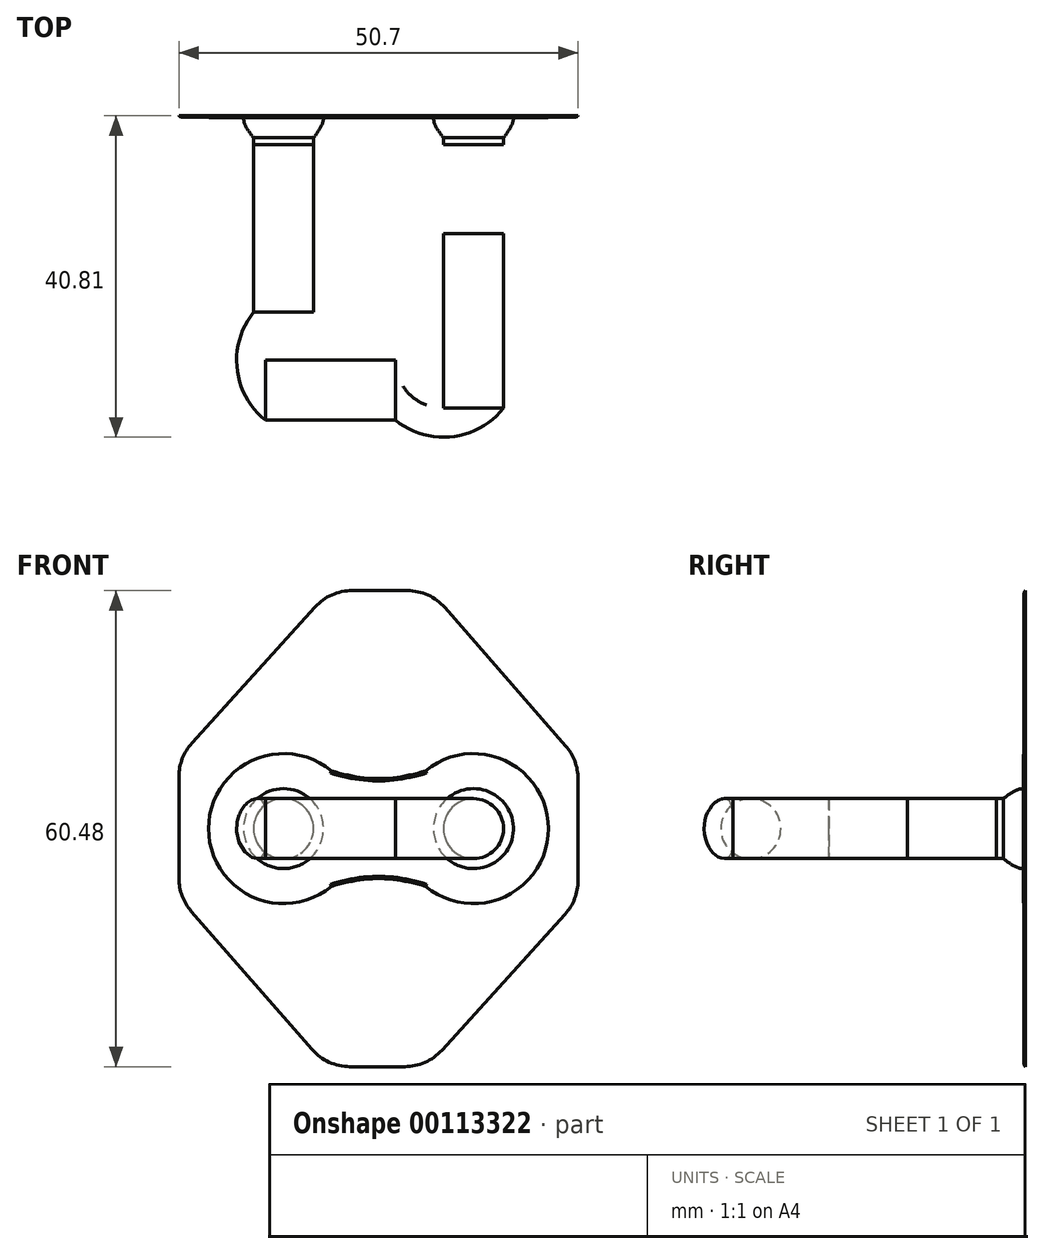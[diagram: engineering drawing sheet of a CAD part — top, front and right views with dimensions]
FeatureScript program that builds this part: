
annotation { "Feature Type Name" : "Feature", "Feature Type Description" : "" }
export const myFeature = defineFeature(function(context is Context, id is Id, definition is map)
    precondition{}
    {
        {
            var Q0;
            Q0=qCreatedBy(makeId("Front.planeOp"),FACE);
            var sketch = newSketch(context, id + "F0", { "sketchPlane" : qUnion([Q0])});
            skLineSegment(sketch, "E0.bottom", {"start": v(-25.35, 30.24) * mm, "end": v(-6.16, 30.24) * mm, "construction": true});
            skLineSegment(sketch, "E0.top", {"start": v(-25.35, -30.24) * mm, "end": v(-6.54, -30.24) * mm, "construction": true});
            skLineSegment(sketch, "E0.left", {"start": v(-25.35, 30.24) * mm, "end": v(-25.35, 9.06) * mm, "construction": true});
            skLineSegment(sketch, "E0.right", {"start": v(25.35, 30.24) * mm, "end": v(25.35, 8.72) * mm, "construction": true});
            skLineSegment(sketch, "E1", {"start": v(-25.35, 30.24) * mm, "end": v(-16.12, 19.24) * mm, "construction": true});
            skLineSegment(sketch, "E2", {"start": v(25.35, 30.24) * mm, "end": v(16.14, 19.25) * mm, "construction": true});
            skLineSegment(sketch, "E3", {"start": v(0, 0) * mm, "end": v(16.12, -19.24) * mm});
            skLineSegment(sketch, "E4", {"start": v(6.54, 30.24) * mm, "end": v(25.35, 30.24) * mm, "construction": true});
            skLineSegment(sketch, "E5", {"start": v(25.35, 6.34) * mm, "end": v(25.35, -6.61) * mm});
            skLineSegment(sketch, "E6", {"start": v(8.44, 28.06) * mm, "end": v(16.14, 19.25) * mm});
            skLineSegment(sketch, "E7", {"start": v(-3.34, 30.24) * mm, "end": v(3.66, 30.24) * mm});
            skLineSegment(sketch, "E8", {"start": v(-25.35, 6.61) * mm, "end": v(-25.35, -6.34) * mm});
            skLineSegment(sketch, "E9", {"start": v(-25.35, -8.72) * mm, "end": v(-25.35, -30.24) * mm, "construction": true});
            skLineSegment(sketch, "E10", {"start": v(-3.66, -30.24) * mm, "end": v(3.34, -30.24) * mm});
            skLineSegment(sketch, "E11", {"start": v(6.16, -30.24) * mm, "end": v(25.35, -30.24) * mm, "construction": true});
            skLineSegment(sketch, "E12", {"start": v(25.35, -9.06) * mm, "end": v(25.35, -30.24) * mm, "construction": true});
            skLineSegment(sketch, "E13", {"start": v(-8.05, 28.15) * mm, "end": v(-16.12, 19.24) * mm});
            skLineSegment(sketch, "E14", {"start": v(-23.78, -10.51) * mm, "end": v(-8.44, -28.06) * mm});
            skLineSegment(sketch, "E15", {"start": v(8.05, -28.15) * mm, "end": v(23.7, -10.88) * mm});
            skLineSegment(sketch, "E16", {"start": v(16.12, -19.24) * mm, "end": v(25.35, -30.24) * mm, "construction": true});
            skLineSegment(sketch, "E17", {"start": v(16.14, 19.25) * mm, "end": v(23.78, 10.51) * mm});
            skLineSegment(sketch, "E18", {"start": v(-16.12, 19.24) * mm, "end": v(-23.7, 10.88) * mm});
            skLineSegment(sketch, "E19", {"start": v(-16.14, -19.25) * mm, "end": v(-25.35, -30.24) * mm, "construction": true});
            skLineSegment(sketch, "E20", {"start": v(-16.12, 19.24) * mm, "end": v(0, 0) * mm});
            skLineSegment(sketch, "E21", {"start": v(16.14, 19.25) * mm, "end": v(-16.14, -19.25) * mm});
            skPoint(sketch, "E22.visualSharp", {"position": v(-6.16, 30.24) * mm});
            skArc(sketch, "E22.filletArc", {"start": v(-3.34, 30.24) * mm, "mid": v(-5.92, 29.7) * mm, "end": v(-8.05, 28.15) * mm});
            skPoint(sketch, "E23.visualSharp", {"position": v(6.54, 30.24) * mm});
            skArc(sketch, "E23.filletArc", {"start": v(8.44, 28.06) * mm, "mid": v(6.28, 29.67) * mm, "end": v(3.66, 30.24) * mm});
            skPoint(sketch, "E24.visualSharp", {"position": v(25.35, 8.72) * mm});
            skArc(sketch, "E24.filletArc", {"start": v(25.35, 6.34) * mm, "mid": v(24.94, 8.57) * mm, "end": v(23.78, 10.51) * mm});
            skPoint(sketch, "E25.visualSharp", {"position": v(25.35, -9.06) * mm});
            skArc(sketch, "E25.filletArc", {"start": v(23.7, -10.88) * mm, "mid": v(24.92, -8.9) * mm, "end": v(25.35, -6.61) * mm});
            skPoint(sketch, "E26.visualSharp", {"position": v(6.16, -30.24) * mm});
            skArc(sketch, "E26.filletArc", {"start": v(3.34, -30.24) * mm, "mid": v(5.92, -29.7) * mm, "end": v(8.05, -28.15) * mm});
            skPoint(sketch, "E27.visualSharp", {"position": v(-6.54, -30.24) * mm});
            skArc(sketch, "E27.filletArc", {"start": v(-8.44, -28.06) * mm, "mid": v(-6.28, -29.67) * mm, "end": v(-3.66, -30.24) * mm});
            skPoint(sketch, "E28.visualSharp", {"position": v(-25.35, -8.72) * mm});
            skArc(sketch, "E28.filletArc", {"start": v(-25.35, -6.34) * mm, "mid": v(-24.94, -8.57) * mm, "end": v(-23.78, -10.51) * mm});
            skPoint(sketch, "E29.visualSharp", {"position": v(-25.35, 9.06) * mm});
            skArc(sketch, "E29.filletArc", {"start": v(-23.7, 10.88) * mm, "mid": v(-24.92, 8.9) * mm, "end": v(-25.35, 6.61) * mm});
            skSolve(sketch);
        }
        {
            assignVariable(context, id + "F1", {"name" : "RealDistance", "anyValue" : .15});
        }
        {
            var Q0;
            Q0=qSketchRegion(id+"F0",true);
            extrude(context, id + "F2", {"entities" : qUnion([Q0]), "depth" : (getVariable(context, 'RealDistance')) * mm});
        }
        {
            assignVariable(context, id + "F3", {"name" : "FilletBase", "anyValue" : .5});
        }
        {
            var Q0;
            Q0=makeQuery(id+"F2.opExtrude","CAP_EDGE",EDGE,{"disambiguationData":[OSD([sQuery(id+"F0.wireOp",EDGE,"E5")])],"isStart":false});
            fillet(context, id + "F4", {"entities" : qUnion([Q0]), "radius" : (getVariable(context, 'FilletBase')) * mm, "tangentPropagation" : true, "allowEdgeOverflow" : false});
        }
        {
            var Q0;
            Q0=makeQuery(id+"F2.opExtrude","CAP_FACE",FACE,{"disambiguationData":[OSD([sQuery(id+"F0.wireOp",EDGE,"E5"),sQuery(id+"F0.wireOp",EDGE,"E6"),sQuery(id+"F0.wireOp",EDGE,"E7"),sQuery(id+"F0.wireOp",EDGE,"E8"),sQuery(id+"F0.wireOp",EDGE,"E10"),sQuery(id+"F0.wireOp",EDGE,"E13"),sQuery(id+"F0.wireOp",EDGE,"E14"),sQuery(id+"F0.wireOp",EDGE,"E15"),sQuery(id+"F0.wireOp",EDGE,"E17"),sQuery(id+"F0.wireOp",EDGE,"E18"),sQuery(id+"F0.wireOp",EDGE,"E22.filletArc"),sQuery(id+"F0.wireOp",EDGE,"E23.filletArc"),sQuery(id+"F0.wireOp",EDGE,"E24.filletArc"),sQuery(id+"F0.wireOp",EDGE,"E25.filletArc"),sQuery(id+"F0.wireOp",EDGE,"E26.filletArc"),sQuery(id+"F0.wireOp",EDGE,"E27.filletArc"),sQuery(id+"F0.wireOp",EDGE,"E28.filletArc"),sQuery(id+"F0.wireOp",EDGE,"E29.filletArc")])],"isStart":false});
            var sketch = newSketch(context, id + "F5", { "sketchPlane" : qUnion([Q0])});
            skCircle(sketch, "E30", {"center": v(-12.06, 0) * mm, "radius": 9.53 * mm});
            skCircle(sketch, "E31", {"center": v(12.07, 0) * mm, "radius": 9.53 * mm});
            skLineSegment(sketch, "E32", {"start": v(0, 6.35) * mm, "end": v(0, -6.35) * mm, "construction": true});
            skLineSegment(sketch, "E33", {"start": v(-12.06, 9.53) * mm, "end": v(0, 9.53) * mm, "construction": true});
            skLineSegment(sketch, "E34", {"start": v(-12.07, -9.53) * mm, "end": v(0, -9.53) * mm, "construction": true});
            skLineSegment(sketch, "E35", {"start": v(-12.06, 9.53) * mm, "end": v(-12.06, 0) * mm, "construction": true});
            skLineSegment(sketch, "E36", {"start": v(-12.07, 0) * mm, "end": v(-12.07, -9.53) * mm, "construction": true});
            skLineSegment(sketch, "E37", {"start": v(12.07, -9.53) * mm, "end": v(12.07, 0) * mm, "construction": true});
            skLineSegment(sketch, "E38", {"start": v(12.07, 9.53) * mm, "end": v(12.07, 0) * mm, "construction": true});
            skLineSegment(sketch, "E39", {"start": v(0, 9.53) * mm, "end": v(12.07, 9.53) * mm, "construction": true});
            skLineSegment(sketch, "E40", {"start": v(0, -9.53) * mm, "end": v(12.07, -9.53) * mm, "construction": true});
            skFitSpline(sketch, "E41", {"points": [v(-12.06, 9.53) * mm, v(0, 6.35) * mm, v(12.07, 9.53) * mm], "startDerivative": vector(24.13, -9.53) * mm, "endDerivative": vector(24.13, 9.52) * mm});
            skFitSpline(sketch, "E42", {"points": [v(-12.07, -9.53) * mm, v(0, -6.35) * mm, v(12.07, -9.53) * mm], "startDerivative": vector(24.13, 9.52) * mm, "endDerivative": vector(24.13, -9.52) * mm});
            skSolve(sketch);
        }
        {
            assignVariable(context, id + "F6", {"name" : "RealDistancePlatform", "anyValue" : .1});
        }
        {
            var Q0;
            Q0=qSketchRegion(id+"F5",true);
            extrude(context, id + "F7", {"entities" : qUnion([Q0]), "operationType" : NewBodyOperationType.ADD, "depth" : (getVariable(context, 'RealDistancePlatform')) * mm});
        }
        {
            var Q0;
            Q0=makeQuery(id+"F7.opExtrude","CAP_EDGE",EDGE,{"disambiguationData":[OSD([sQuery(id+"F5.wireOp",EDGE,"E31")])],"isStart":false});
            var Q1;
            Q1=makeQuery(id+"F7.opExtrude","CAP_EDGE",EDGE,{"disambiguationData":[OSD([sQuery(id+"F5.wireOp",EDGE,"E42")])],"isStart":false});
            var Q2;
            Q2=makeQuery(id+"F7.opExtrude","CAP_EDGE",EDGE,{"disambiguationData":[OSD([sQuery(id+"F5.wireOp",EDGE,"E30")])],"isStart":false});
            var Q3;
            Q3=makeQuery(id+"F7.opExtrude","CAP_EDGE",EDGE,{"disambiguationData":[OSD([sQuery(id+"F5.wireOp",EDGE,"E41")])],"isStart":false});
            fillet(context, id + "F8", {"entities" : qUnion([Q0, Q1, Q2, Q3]), "radius" : (getVariable(context, 'FilletBase')) * mm, "tangentPropagation" : true, "allowEdgeOverflow" : false});
        }
        {
            var Q0;
            Q0=makeQuery(id+"F7.opExtrude","CAP_FACE",FACE,{"disambiguationData":[OSD([sQuery(id+"F5.wireOp",EDGE,"E30"),sQuery(id+"F5.wireOp",EDGE,"E31"),sQuery(id+"F5.wireOp",EDGE,"E41"),sQuery(id+"F5.wireOp",EDGE,"E42")])],"isStart":false});
            var sketch = newSketch(context, id + "F9", { "sketchPlane" : qUnion([Q0])});
            skCircle(sketch, "E43", {"center": v(-12.06, 0) * mm, "radius": 5.08 * mm});
            skCircle(sketch, "E44", {"center": v(12.07, 0) * mm, "radius": 5.08 * mm});
            skSolve(sketch);
        }
        {
            var Q0;
            Q0=makeQuery(id+"F9.imprint","IMPRINT",FACE,{"disambiguationData":[TD([[makeQuery(id+"F9.imprint","IMPRINT",EDGE,{"derivedFrom":sQuery(id+"F9.wireOp",EDGE,"E43")}),-1.0]])]});
            cPlane(context, id + "F10", {"entities" : qUnion([Q0]), "cplaneType" : CPlaneType.OFFSET, "offset" : 2.54 * mm, "width" : 152.4 * mm, "height" : 152.4 * mm});
        }
        {
            var Q0;
            Q0=qCreatedBy(id+"F10.planeOp",FACE);
            var sketch = newSketch(context, id + "F11", { "sketchPlane" : qUnion([Q0])});
            skCircle(sketch, "E45", {"center": v(-12.06, 0) * mm, "radius": 3.81 * mm});
            skCircle(sketch, "E46", {"center": v(12.07, 0) * mm, "radius": 3.81 * mm});
            skSolve(sketch);
        }
        {
            var Q0;
            Q0=makeQuery(id+"F9.imprint","IMPRINT",FACE,{"disambiguationData":[TD([[makeQuery(id+"F9.imprint","IMPRINT",EDGE,{"derivedFrom":sQuery(id+"F9.wireOp",EDGE,"E43")}),1.0]])]});
            var Q1;
            Q1=makeQuery(id+"F11.imprint","IMPRINT",FACE,{"disambiguationData":[TD([[makeQuery(id+"F11.imprint","IMPRINT",EDGE,{"derivedFrom":sQuery(id+"F11.wireOp",EDGE,"E45")}),1.0]])]});
            loft(context, id + "F12", {"startCondition" : LoftEndDerivativeType.NORMAL_TO_PROFILE, "startMagnitude" : 1, "sheetProfilesArray" : [{ "sheetProfileEntities" : qUnion([Q0]) }, { "sheetProfileEntities" : qUnion([Q1]) }]});
        }
        {
            var Q1;
            Q1=makeQuery(id+"F9.imprint","IMPRINT",FACE,{"disambiguationData":[TD([[makeQuery(id+"F9.imprint","IMPRINT",EDGE,{"derivedFrom":sQuery(id+"F9.wireOp",EDGE,"E44")}),1.0]])]});
            var Q2;
            Q2=makeQuery(id+"F11.imprint","IMPRINT",FACE,{"disambiguationData":[TD([[makeQuery(id+"F11.imprint","IMPRINT",EDGE,{"derivedFrom":sQuery(id+"F11.wireOp",EDGE,"E46")}),1.0]])]});
            loft(context, id + "F13", {"operationType" : NewBodyOperationType.ADD, "startCondition" : LoftEndDerivativeType.NORMAL_TO_PROFILE, "startMagnitude" : 1, "sheetProfilesArray" : [{ "sheetProfileEntities" : qUnion([Q1]) }, { "sheetProfileEntities" : qUnion([Q2]) }]});
        }
        {
            assignVariable(context, id + "F14", {"name" : "ExLockBar", "anyValue" : .8725});
        }
        {
            var Q0;
            Q0=makeQuery(id+"F13.opLoft","CAP_FACE",FACE,{"disambiguationData":[OSD([makeQuery(id+"F11.imprint","IMPRINT",FACE,{"disambiguationData":[TD([[makeQuery(id+"F11.imprint","IMPRINT",EDGE,{"derivedFrom":sQuery(id+"F11.wireOp",EDGE,"E46")}),1.0]])]})])],"isStart":true});
            var Q1;
            Q1=makeQuery(id+"F12.opLoft","CAP_FACE",FACE,{"disambiguationData":[OSD([makeQuery(id+"F11.imprint","IMPRINT",FACE,{"disambiguationData":[TD([[makeQuery(id+"F11.imprint","IMPRINT",EDGE,{"derivedFrom":sQuery(id+"F11.wireOp",EDGE,"E45")}),1.0]])]})])],"isStart":true});
            extrude(context, id + "F15", {"entities" : qUnion([Q0, Q1]), "depth" : (getVariable(context, 'ExLockBar')) * mm});
        }
        {
            var Q0;
            Q0=qCreatedBy(makeId("Top.planeOp"),FACE);
            var sketch = newSketch(context, id + "F16", { "sketchPlane" : qUnion([Q0])});
            skLineSegment(sketch, "E47", {"start": v(-8.25, -8.89) * mm, "end": v(-8.25, -31.05) * mm, "construction": true});
            skLineSegment(sketch, "E48", {"start": v(-15.88, -31.05) * mm, "end": v(-15.88, -8.89) * mm, "construction": true});
            skLineSegment(sketch, "E49", {"start": v(15.88, -8.9) * mm, "end": v(15.88, -31.05) * mm, "construction": true});
            skLineSegment(sketch, "E50", {"start": v(8.26, -31.05) * mm, "end": v(8.26, -8.89) * mm, "construction": true});
            skLineSegment(sketch, "E51", {"start": v(-15.88, -31.05) * mm, "end": v(-12.06, -31.05) * mm});
            skLineSegment(sketch, "E52", {"start": v(8.25, -31.05) * mm, "end": v(12.07, -31.05) * mm});
            skLineSegment(sketch, "E53", {"start": v(8.25, -31.05) * mm, "end": v(4.13, -31.05) * mm});
            skLineSegment(sketch, "E54", {"start": v(-12.06, -31.05) * mm, "end": v(-8.25, -31.05) * mm});
            skLineSegment(sketch, "E55", {"start": v(12.07, -31.05) * mm, "end": v(15.88, -31.05) * mm});
            skLineSegment(sketch, "E56", {"start": v(0, -31.05) * mm, "end": v(-4.13, -31.05) * mm});
            skLineSegment(sketch, "E57", {"start": v(-8.25, -8.9) * mm, "end": v(8.26, -8.9) * mm});
            skLineSegment(sketch, "E58", {"start": v(0, -31.05) * mm, "end": v(0, -31.05) * mm});
            skLineSegment(sketch, "E59", {"start": v(-15.88, -8.9) * mm, "end": v(-12.07, -8.9) * mm, "construction": true});
            skLineSegment(sketch, "E60", {"start": v(15.88, -8.9) * mm, "end": v(12.07, -8.9) * mm, "construction": true});
            skLineSegment(sketch, "E61", {"start": v(-12.07, -8.9) * mm, "end": v(-8.25, -8.9) * mm, "construction": true});
            skLineSegment(sketch, "E62", {"start": v(12.07, -8.9) * mm, "end": v(8.26, -8.9) * mm, "construction": true});
            skLineSegment(sketch, "E63", {"start": v(-12.07, -31.05) * mm, "end": v(-12.07, -8.9) * mm});
            skLineSegment(sketch, "E64", {"start": v(12.07, -31.05) * mm, "end": v(12.07, -19.97) * mm});
            skLineSegment(sketch, "E65", {"start": v(12.07, -19.97) * mm, "end": v(12.07, -8.9) * mm});
            skLineSegment(sketch, "E66", {"start": v(-4.13, -31.05) * mm, "end": v(-8.25, -31.05) * mm});
            skLineSegment(sketch, "E67", {"start": v(4.13, -31.05) * mm, "end": v(0, -31.05) * mm});
            skLineSegment(sketch, "E68", {"start": v(-8.25, -31.05) * mm, "end": v(-8.25, -31.05) * mm});
            skLineSegment(sketch, "E69", {"start": v(8.26, -31.05) * mm, "end": v(8.26, -31.05) * mm});
            skArc(sketch, "E70", {"start": v(12.07, -31.05) * mm, "mid": v(10.95, -33.75) * mm, "end": v(8.26, -34.86) * mm});
            skArc(sketch, "E71", {"start": v(-12.06, -31.05) * mm, "mid": v(-10.95, -33.75) * mm, "end": v(-8.25, -34.86) * mm});
            skLineSegment(sketch, "E72", {"start": v(8.26, -34.86) * mm, "end": v(-8.25, -34.86) * mm});
            skSolve(sketch);
        }
        {
            var Q0;
            Q0=makeQuery(id+"F11.imprint","IMPRINT",FACE,{"disambiguationData":[TD([[makeQuery(id+"F11.imprint","IMPRINT",EDGE,{"derivedFrom":sQuery(id+"F11.wireOp",EDGE,"E45")}),1.0]])]});
            var Q1;
            Q1=sQuery(id+"F16.wireOp",EDGE,"E63");
            var Q2;
            Q2=sQuery(id+"F16.wireOp",EDGE,"E71");
            var Q3;
            Q3=sQuery(id+"F16.wireOp",EDGE,"E72");
            var Q4;
            Q4=sQuery(id+"F16.wireOp",EDGE,"E70");
            var Q5;
            Q5=sQuery(id+"F16.wireOp",EDGE,"E64");
            var Q6;
            Q6=sQuery(id+"F16.wireOp",EDGE,"E65");
            sweep(context, id + "F17", {"profiles" : qUnion([Q0]), "path" : qUnion([Q1, Q2, Q3, Q4, Q5, Q6])});
        }
    });
